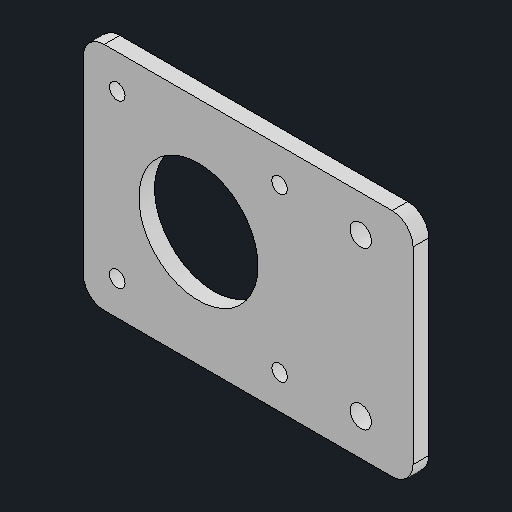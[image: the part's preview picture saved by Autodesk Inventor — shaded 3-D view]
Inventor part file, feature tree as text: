
AUTODESK INVENTOR PART (.ipt)
format: ipt  version: 2024.2 (Build 282272000, 272)  size: 97,280 bytes
history: native  units: mm
features: other x1, fillet x1
ambient origin geometry x8: Origin, YZ Plane, XZ Plane, XY Plane, X Axis, Y Axis, Z Axis, Center Point
bodies: Body1 (feature_tree)
feature tree (2):
  other  "솔리드1"
  fillet  "Fillet1"  [1 undecoded]
note: 1 required parameter value undecoded (feature->parameter linkage not recoverable at this tier; creation-order binding heuristic only, values carry confidence <= 0.55)
